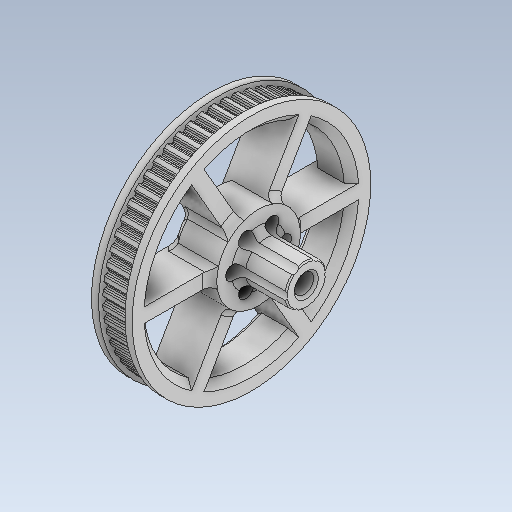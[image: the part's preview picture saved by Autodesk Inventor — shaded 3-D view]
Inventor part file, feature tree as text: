
AUTODESK INVENTOR PART (.ipt)
format: ipt  version: 2020 (Build 240168000, 168)  size: 2,100,224 bytes
history: native  units: mm
features: extrude x10, sketch x10, chamfer x5, projected_geometry x5, other x4, thicken_offset x3, fillet x3, plane x2, pattern_circular x2, reference x2
ambient origin geometry x8: Origin, YZ Plane, XZ Plane, XY Plane, X Axis, Y Axis, Z Axis, Center Point
bodies: Solid1 (feature_tree)
feature tree (46):
  plane  "Work Plane1"
  extrude  "Extrusion1"  Depth=110.0mm
  plane  "Work Plane2"
  extrude  "Extrusion2"  [1 undecoded]
  extrude  "Extrusion3"  Depth=20.0mm TaperAngle=0.0deg
  thicken_offset  "Thicken1"
  extrude  "Extrusion4"  Depth=10.0mm
  extrude  "Extrusion5"  Depth=20.0mm TaperAngle=0.0deg
  extrude  "Extrusion6"  Depth=3.0mm TaperAngle=0.0deg
  thicken_offset  "Thicken9"
  thicken_offset  "Thicken10"
  extrude  "Extrusion15"  Depth=3.0mm
  extrude  "Extrusion18"  Depth=1.0mm
  pattern_circular  "Circular Pattern2"  [2 undecoded]
  extrude  "Extrusion19"  Depth=3.0mm
  pattern_circular  "Circular Pattern3"  [2 undecoded]
  fillet  "Fillet7"  Radius=60.0mm
  chamfer  "Chamfer8"  Distance=93.0mm
  chamfer  "Chamfer9"  Distance=84.0mm
  fillet  "Fillet9"  Radius=6.0mm
  chamfer  "Chamfer10"  Distance=26.0mm
  extrude  "Extrusion20"  Depth=3.0mm TaperAngle=0.0deg
  fillet  "Fillet10"  [1 undecoded]
  chamfer  "Chamfer11"  Distance=6.0mm
  chamfer  "Chamfer12"  Distance=26.0mm
  sketch  "Sketch1"  dims[d0=0.0mm d1=110.0mm]
  sketch  "Sketch2"  dims[d2=10.0mm d3=0.0mm d4=-1.0mm]
  sketch  "Sketch3"  dims[d5=110.0mm d6=20.0mm d7=0.0mm]
  projected_geometry  "Projected Loop1"
  sketch  "Sketch4"  dims[d8=20.0mm d9=0.0mm d10=10.0mm d11=9.0mm]
  projected_geometry  "Projected Loop2"
  sketch  "Sketch5"  dims[d12=8.15mm d13=20.0mm d14=0.0mm]
  sketch  "Sketch6"  dims[d15=102.0mm d16=3.0mm d17=0.0mm]
  sketch  "Sketch19"  dims[d18=3.0mm d19=0.0mm d143=1.0mm]
  projected_geometry  "Projected Loop15"
  sketch  "Sketch23"  dims[d144=1.0mm d145=1.0mm]
  reference  "Reference4"
  reference  "Reference5"
  sketch  "Sketch24"  dims[d146=1.0mm]
  projected_geometry  "Projected Loop17"
  sketch  "Sketch25"  dims[d164=35.0mm d165=3.0mm d166=0.0mm d176=6.0mm d177=25.0mm d178=0.0mm d179=60.0mm d180=62.831853mm d182=93.0mm d183=84.0mm d184=6.0mm d185=26.0mm d186=60.0mm d188=0.0mm d190=60.0deg d191=6.0mm d192=26.0mm d193=25.0mm d194=0.0mm d195=60.0mm d196=62.831853mm d198=3.0mm d199=3.0mm d200=2.0mm d201=45.0deg d206=3.0mm d207=2.0mm d208=45.0deg d209=3.0mm d213=1.0mm d214=2.0mm d215=45.0deg d216=17.0mm d217=20.0mm d218=0.0mm d219=3.0mm d220=0.5mm d221=2.0mm d222=45.0deg d223=1.0mm d224=2.0mm d225=45.0deg]
  projected_geometry  "Projected Loop18"
  other  "_ATP60XL037-A-C12_b"
  parser-record x1  (decoder bookkeeping rows leaked as tree rows — omitted from the tree; the rows remain in map.json)
  other  "xl_wheel_ass.iam"
  other  "xl_20_ori:1"
note: 6 required parameter values undecoded (feature->parameter linkage not recoverable at this tier; creation-order binding heuristic only, values carry confidence <= 0.55)
note: 1 file-system path scrubbed to <path> (originals preserved in map.json)
